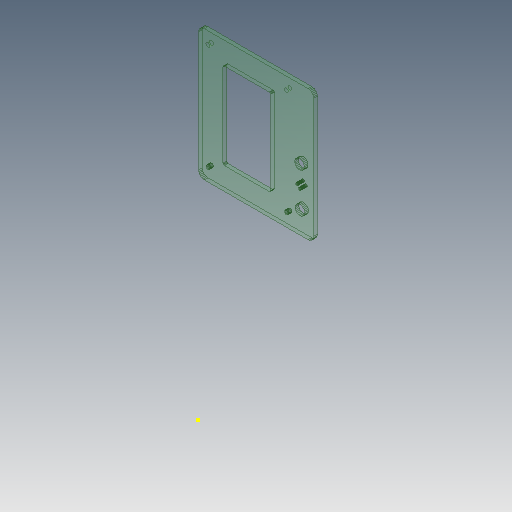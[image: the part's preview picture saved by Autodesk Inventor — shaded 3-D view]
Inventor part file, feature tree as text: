
AUTODESK INVENTOR PART (.ipt)
format: ipt  version: 2017 (Build 210142000, 142)  size: 434,688 bytes
history: native  units: mm
features: sketch x4, extrude x3, other x3, reference x1
ambient origin geometry x8: Origin, YZ Plane, XZ Plane, XY Plane, X Axis, Y Axis, Z Axis, Center Point
bodies: Solid1 (feature_tree)
feature tree (11):
  extrude  "Extrusion1"  Depth=3.0mm
  extrude  "Extrusion2"  Depth=10.0mm TaperAngle=0.0deg
  extrude  "Extrusion3"  [1 undecoded]
  sketch  "Sketch4"
  sketch  "Sketch1"  dims[d0=3.0mm d1=0.0mm d2=3.4mm]
  sketch  "Sketch2"  dims[d3=3.0mm d4=0.0mm d5=10.0mm d6=0.0mm]
  sketch  "Sketch3"
  reference  "Reference1"
  parser-record x1  (decoder bookkeeping rows leaked as tree rows — omitted from the tree; the rows remain in map.json)
  other  "LCD-Mount.iam"
  other  "Full Graphic Smart Controller:1"
note: 1 required parameter value undecoded (feature->parameter linkage not recoverable at this tier; creation-order binding heuristic only, values carry confidence <= 0.55)
note: 1 file-system path scrubbed to <path> (originals preserved in map.json)
